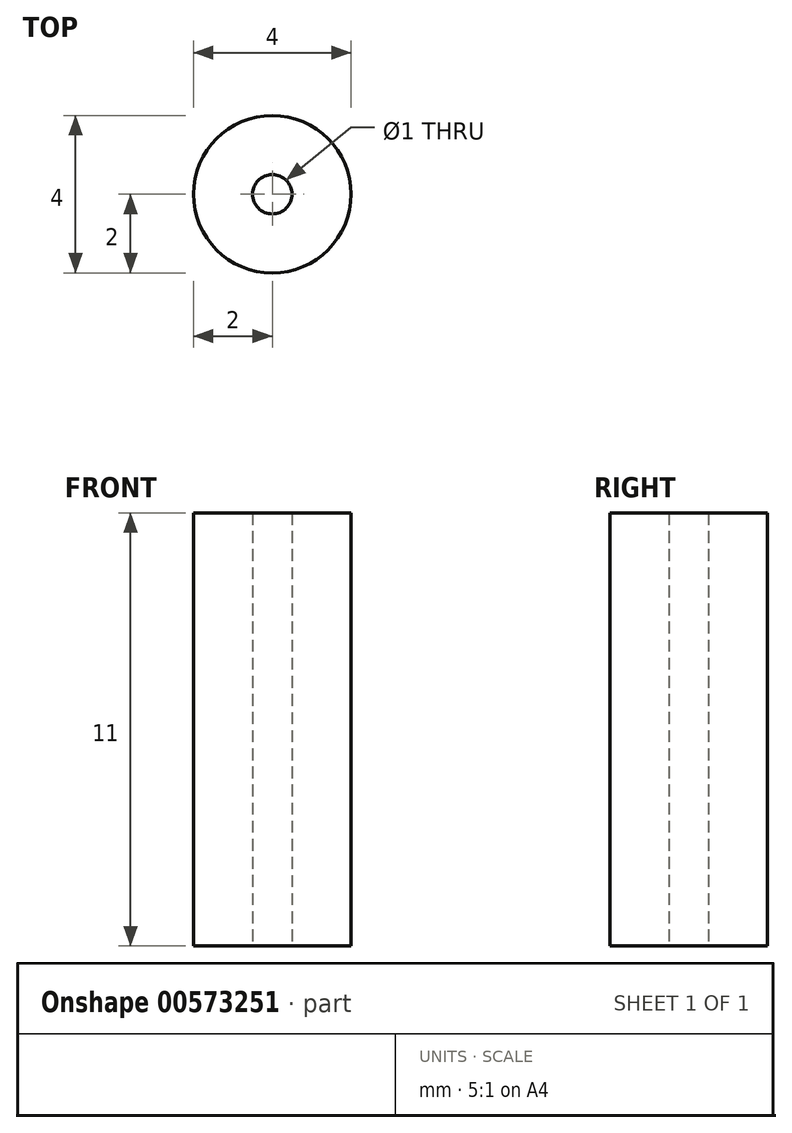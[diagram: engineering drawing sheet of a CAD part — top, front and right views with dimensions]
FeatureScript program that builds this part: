
annotation { "Feature Type Name" : "Feature", "Feature Type Description" : "" }
export const myFeature = defineFeature(function(context is Context, id is Id, definition is map)
    precondition{}
    {
        {
            var Q0;
            Q0=qCreatedBy(makeId("Top.planeOp"),FACE);
            var sketch = newSketch(context, id + "F0", { "sketchPlane" : qUnion([Q0])});
            skCircle(sketch, "E0", {"center": v(0, 0) * mm, "radius": 2 * mm});
            skCircle(sketch, "E1", {"center": v(0, 0) * mm, "radius": 0.5 * mm});
            skSolve(sketch);
        }
        {
            var Q0;
            Q0=makeQuery(id+"F0.imprint","IMPRINT",FACE,{"disambiguationData":[TD([[makeQuery(id+"F0.imprint","IMPRINT",EDGE,{"derivedFrom":sQuery(id+"F0.wireOp",EDGE,"E0")}),1.0]])]});
            extrude(context, id + "F1", {"entities" : qUnion([Q0]), "depth" : 11 * mm, "offsetDistance" : 25 * mm});
        }
    });
